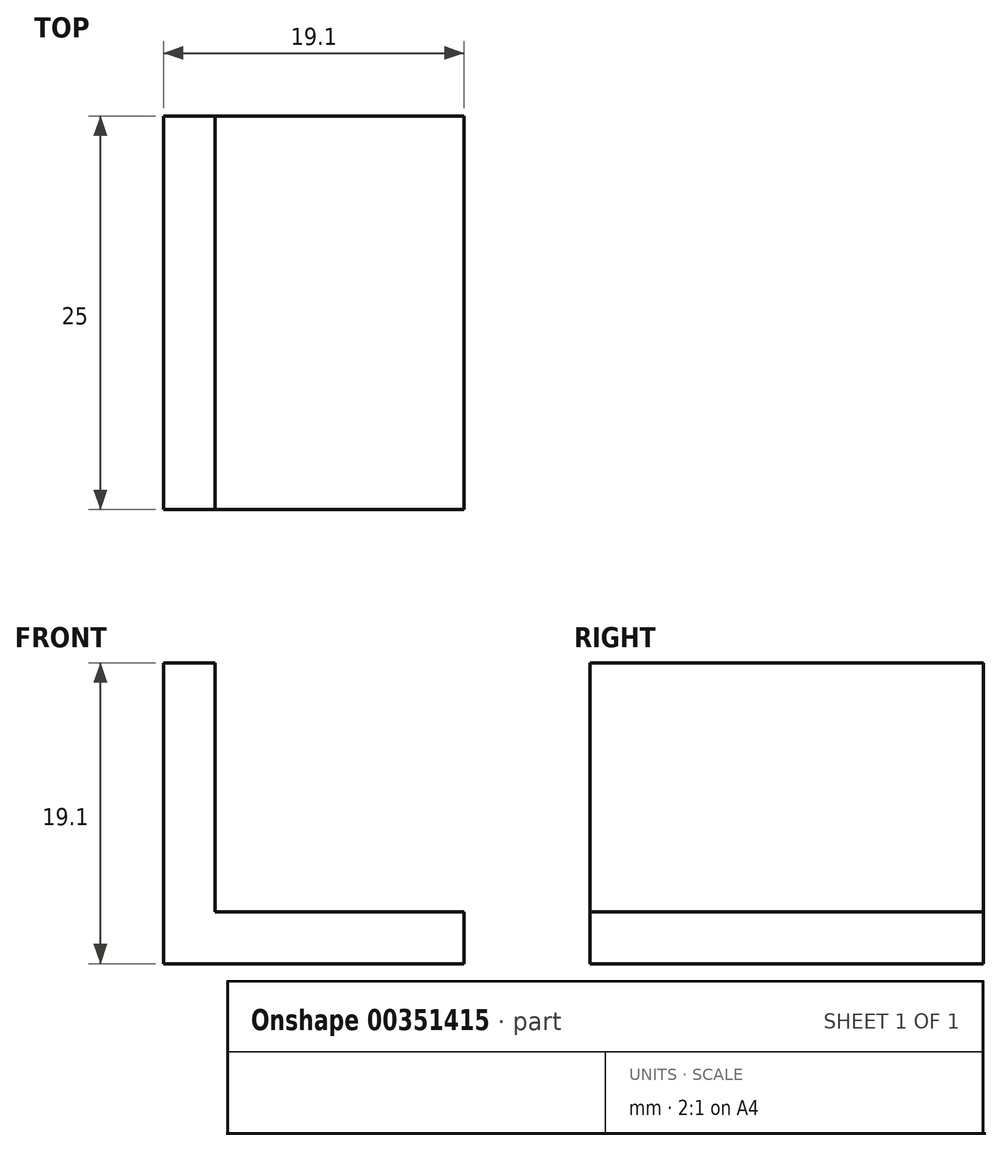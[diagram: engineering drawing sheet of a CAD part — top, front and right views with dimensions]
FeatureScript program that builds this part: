
annotation { "Feature Type Name" : "Feature", "Feature Type Description" : "" }
export const myFeature = defineFeature(function(context is Context, id is Id, definition is map)
    precondition{}
    {
        {
            var Q0;
            Q0=qCreatedBy(makeId("Front.planeOp"),FACE);
            var sketch = newSketch(context, id + "F0", { "sketchPlane" : qUnion([Q0])});
            skLineSegment(sketch, "E0.bottom", {"start": v(0, 0) * mm, "end": v(-3.3, 0) * mm});
            skLineSegment(sketch, "E0.top", {"start": v(0, 19.1) * mm, "end": v(-3.3, 19.1) * mm});
            skLineSegment(sketch, "E0.left", {"start": v(0, 0) * mm, "end": v(0, 19.1) * mm});
            skLineSegment(sketch, "E0.right", {"start": v(-3.3, 0) * mm, "end": v(-3.3, 19.1) * mm});
            skLineSegment(sketch, "E1.bottom", {"start": v(0, 0) * mm, "end": v(15.8, 0) * mm});
            skLineSegment(sketch, "E1.top", {"start": v(0, 3.3) * mm, "end": v(15.8, 3.3) * mm});
            skLineSegment(sketch, "E1.left", {"start": v(0, 0) * mm, "end": v(0, 3.3) * mm});
            skLineSegment(sketch, "E1.right", {"start": v(15.8, 0) * mm, "end": v(15.8, 3.3) * mm});
            skSolve(sketch);
        }
        {
            var Q0;
            Q0 = qSketchRegion(id + "F0", true);
            extrude(context, id + "F1", {"entities" : qUnion([Q0]), "depth" : 25 * mm});
        }
    });
